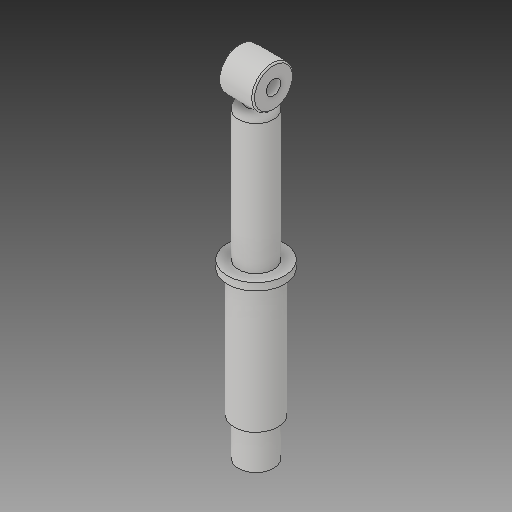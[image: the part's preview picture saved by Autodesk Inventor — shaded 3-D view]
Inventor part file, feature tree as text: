
AUTODESK INVENTOR PART (.ipt)
format: ipt  version: 2018 (Build 220112000, 112)  size: 151,552 bytes
history: native  units: mm
features: sketch x7, extrude x5, fillet x3, hole x2, other x1
ambient origin geometry x8: Origin, YZ Plane, XZ Plane, XY Plane, X Axis, Y Axis, Z Axis, Center Point
bodies: Body1 (feature_tree)
feature tree (18):
  other  "ソリッド1"
  extrude  "押し出し1"  Depth=24.0mm
  extrude  "押し出し2"  Depth=94.0mm TaperAngle=0.0deg
  hole  "穴1"  [1 undecoded]
  fillet  "フィレット2"  Radius=14.1mm
  fillet  "フィレット3"  Radius=24.0mm
  fillet  "フィレット4"  Radius=5.0mm
  extrude  "押し出し3"  Depth=1.0mm
  extrude  "押し出し4"  Depth=1.0mm
  extrude  "押し出し5"  Depth=39.0mm
  hole  "穴2"  [1 undecoded]
  sketch  "スケッチ1"
  sketch  "スケッチ3"
  sketch  "スケッチ4"
  sketch  "スケッチ5"
  sketch  "スケッチ6"
  sketch  "スケッチ7"
  sketch  "スケッチ8"
note: 2 required parameter values undecoded (feature->parameter linkage not recoverable at this tier; creation-order binding heuristic only, values carry confidence <= 0.55)
